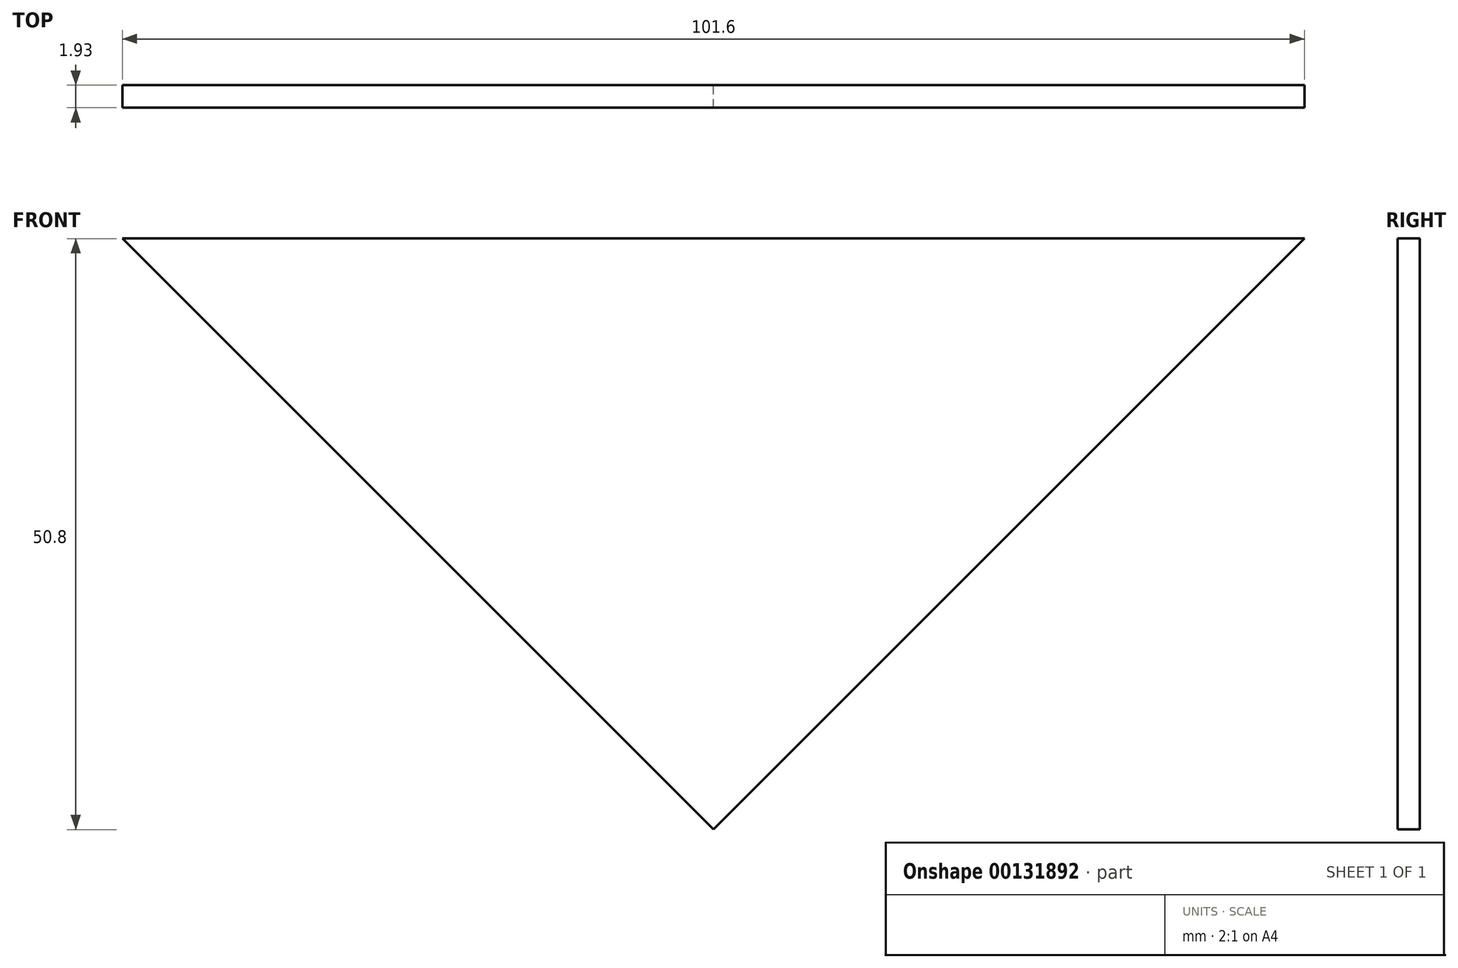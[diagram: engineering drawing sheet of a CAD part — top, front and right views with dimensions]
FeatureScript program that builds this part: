
annotation { "Feature Type Name" : "Feature", "Feature Type Description" : "" }
export const myFeature = defineFeature(function(context is Context, id is Id, definition is map)
    precondition{}
    {
        {
            var Q0;
            Q0=qCreatedBy(makeId("Front.planeOp"),FACE);
            var sketch = newSketch(context, id + "F0", { "sketchPlane" : qUnion([Q0])});
            skLineSegment(sketch, "E0", {"start": v(-50.8, 35.44) * mm, "end": v(50.8, 35.44) * mm});
            skLineSegment(sketch, "E1", {"start": v(0, -15.36) * mm, "end": v(-50.8, 35.44) * mm});
            skLineSegment(sketch, "E2", {"start": v(50.8, 35.44) * mm, "end": v(0, -15.36) * mm});
            skSolve(sketch);
        }
        {
            var Q0;
            Q0 = qSketchRegion(id + "F0", true);
            extrude(context, id + "F1", {"entities" : qUnion([Q0]), "depth" : 1.93 * mm});
        }
    });
